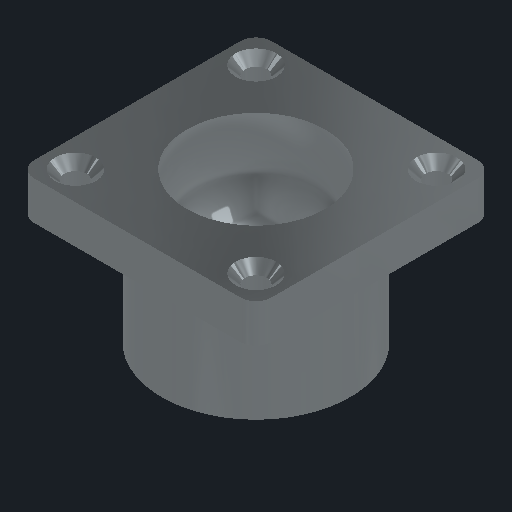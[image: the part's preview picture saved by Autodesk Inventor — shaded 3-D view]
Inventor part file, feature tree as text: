
AUTODESK INVENTOR PART (.ipt)
format: ipt  version: 2022 (Build 260153000, 153)  size: 167,936 bytes
history: native  units: mm (DEFAULTED — no unit token found)
features: other x8, sketch x4, extrude x3, fillet x1, plane x1, revolve x1, chamfer x1, projected_geometry x1
bodies: Body1 (feature_tree)
feature tree (20):
  other  "Sólido1"
  other  "Origen"
  extrude  "Extrusión1"  Depth=48.2mm TaperAngle=0.0deg
  extrude  "Extrusión2"  Depth=12.4mm TaperAngle=0.0deg
  extrude  "Extrusión3"  Depth=7.1mm
  fillet  "Empalme1"  [1 undecoded]
  plane  "Plano de trabajo1"
  revolve  "Revolución1"  [1 undecoded]
  chamfer  "Chamfer1"  Distance=50.8mm
  other  "Plano YZ"
  other  "Plano XZ"
  other  "Plano XY"
  other  "Eje X"
  other  "Eje Y"
  other  "Eje Z"
  sketch  "Boceto1"  dims[d0=60.5mm d1=48.2mm d2=0.0mm]
  sketch  "Boceto2"  dims[d3=76.2mm d4=12.4mm d5=0.0mm]
  sketch  "Boceto3"  dims[d7=57.9mm d8=7.1mm d9=0.0mm d10=0.0mm]
  projected_geometry  "Contorno proyectado1"
  sketch  "Boceto4"  dims[d11=5.0mm d12=-35.8mm d13=50.8mm d14=360.0deg d15=3.0mm d16=2.0mm d17=45.0deg]
note: 2 required parameter values undecoded (feature->parameter linkage not recoverable at this tier; creation-order binding heuristic only, values carry confidence <= 0.55)